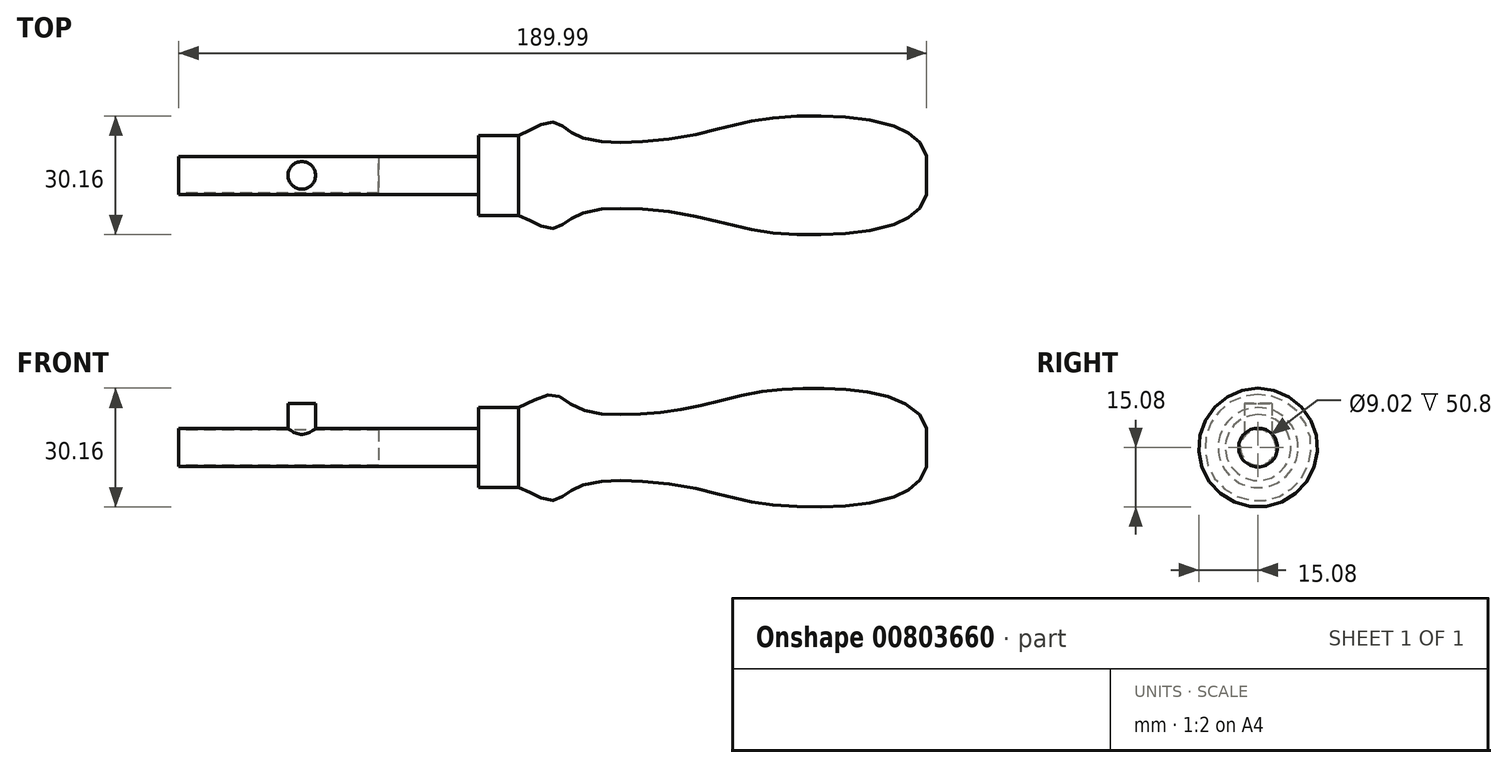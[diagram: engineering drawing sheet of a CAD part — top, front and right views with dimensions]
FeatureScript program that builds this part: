
annotation { "Feature Type Name" : "Feature", "Feature Type Description" : "" }
export const myFeature = defineFeature(function(context is Context, id is Id, definition is map)
    precondition{}
    {
        {
            var Q0;
            Q0=qCreatedBy(makeId("Front.planeOp"),FACE);
            var sketch = newSketch(context, id + "F0", { "sketchPlane" : qUnion([Q0])});
            skLineSegment(sketch, "E0", {"start": v(-76.2, 0) * mm, "end": v(-76.2, 4.83) * mm});
            skLineSegment(sketch, "E1", {"start": v(-76.2, 4.83) * mm, "end": v(0, 4.83) * mm});
            skLineSegment(sketch, "E2", {"start": v(0, 4.83) * mm, "end": v(0, 0) * mm});
            skLineSegment(sketch, "E3", {"start": v(0, 0) * mm, "end": v(0, 10.16) * mm});
            skLineSegment(sketch, "E4", {"start": v(0, 10.16) * mm, "end": v(10.16, 10.16) * mm});
            skLineSegment(sketch, "E5", {"start": v(10.16, 10.16) * mm, "end": v(10.16, 0) * mm});
            skLineSegment(sketch, "E6", {"start": v(-76.2, 0) * mm, "end": v(113.8, 0) * mm});
            skLineSegment(sketch, "E7", {"start": v(18.8, 0) * mm, "end": v(53.85, 0) * mm});
            skFitSpline(sketch, "E8", {"points": [v(10.16, 10.16) * mm, v(18.8, 13.5) * mm, v(24.9, 10.16) * mm, v(37.49, 8.41) * mm, v(53.85, 10.16) * mm, v(70.77, 14.03) * mm, v(87.95, 15.03) * mm, v(105.83, 12.34) * mm, v(113.8, 4.93) * mm], "startDerivative": vector(101.95, 39.94) * mm, "endDerivative": vector(20.63, -90.04) * mm});
            skLineSegment(sketch, "E9", {"start": v(113.8, 0) * mm, "end": v(113.8, 4.93) * mm});
            skSolve(sketch);
        }
        {
            var Q0;
            Q0 = qSketchRegion(id + "F0", true);
            var Q1;
            Q1=sQuery(id+"F0.wireOp",EDGE,"E6");
            revolve(context, id + "F1", {"surfaceOperationType" : NewSurfaceOperationType.NEW, "entities" : qUnion([Q0]), "axis" : qUnion([Q1]), "revolveType" : RevolveType.FULL});
        }
        {
            var Q0;
            Q0=qCreatedBy(makeId("Top.planeOp"),FACE);
            var sketch = newSketch(context, id + "F2", { "sketchPlane" : qUnion([Q0])});
            skLineSegment(sketch, "E10.0", {"start": v(-76.2, 0) * mm, "end": v(113.8, 0) * mm});
            skCircle(sketch, "E11", {"center": v(-44.96, 0) * mm, "radius": 3.5 * mm});
            skSolve(sketch);
        }
        {
            var Q0;
            {var subQ0=sQuery(id+"F2.wireOp",EDGE,"E11");var subQ1=sQuery(id+"F2.wireOp",EDGE,"E10.0");var subQ2=makeQuery(id+"F2.imprint","INTERSECT",VERTEX,{"disambiguationData":[OD(0.0)],"derivedFrom":[subQ1,subQ0]});Q0=makeQuery(id+"F2.imprint","IMPRINT",FACE,{"disambiguationData":[TD([[makeQuery(id+"F2.imprint","IMPRINT",EDGE,{"disambiguationData":[TD([[subQ2,-1.0]])],"derivedFrom":subQ1}),1.0]])]});}
            var Q1;
            {var subQ0=sQuery(id+"F2.wireOp",EDGE,"E11");var subQ1=sQuery(id+"F2.wireOp",EDGE,"E10.0");var subQ2=makeQuery(id+"F2.imprint","INTERSECT",VERTEX,{"disambiguationData":[OD(0.0)],"derivedFrom":[subQ1,subQ0]});Q1=makeQuery(id+"F2.imprint","IMPRINT",FACE,{"disambiguationData":[TD([[makeQuery(id+"F2.imprint","IMPRINT",EDGE,{"disambiguationData":[TD([[subQ2,-1.0]])],"derivedFrom":subQ1}),-1.0]])]});}
            extrude(context, id + "F3", {"entities" : qUnion([Q0, Q1]), "operationType" : NewBodyOperationType.ADD, "depth" : 11.18 * mm, "offsetDistance" : 25.4 * mm});
        }
        {
            var Q0;
            Q0=makeQuery(id+"F1.opRevolve","SWEPT_FACE",FACE,{"disambiguationData":[OSD([sQuery(id+"F0.wireOp",EDGE,"E0")])]});
            var sketch = newSketch(context, id + "F4", { "sketchPlane" : qUnion([Q0])});
            skCircle(sketch, "E12", {"center": v(0, 0) * mm, "radius": 4.5 * mm});
            skSolve(sketch);
        }
        {
            var Q0;
            Q0=makeQuery(id+"F4.imprint","IMPRINT",FACE,{"disambiguationData":[TD([[makeQuery(id+"F4.imprint","IMPRINT",EDGE,{"derivedFrom":sQuery(id+"F4.wireOp",EDGE,"E12")}),1.0]])]});
            extrude(context, id + "F5", {"entities" : qUnion([Q0]), "oppositeDirection" : true, "depth" : 50.8 * mm, "offsetDistance" : 25.4 * mm});
        }
        {
            var Q0;
            Q0=makeQuery(id+"F5.opExtrude","SWEPT_BODY",BODY,{"disambiguationData":[OSD([sQuery(id+"F4.wireOp",EDGE,"E12")])]});
            var Q1;
            Q1=makeQuery(id+"F1.opRevolve","SWEPT_BODY",BODY,{"disambiguationData":[OSD([sQuery(id+"F0.wireOp",EDGE,"E0"),sQuery(id+"F0.wireOp",EDGE,"E1"),sQuery(id+"F0.wireOp",EDGE,"E3"),sQuery(id+"F0.wireOp",EDGE,"E4"),sQuery(id+"F0.wireOp",EDGE,"E6"),sQuery(id+"F0.wireOp",EDGE,"E7"),sQuery(id+"F0.wireOp",EDGE,"E8"),sQuery(id+"F0.wireOp",EDGE,"E9")])]});
            booleanBodies(context, id + "F6", {"operationType" : BooleanOperationType.SUBTRACTION, "tools" : qUnion([Q0]), "targets" : qUnion([Q1])});
        }
    });
